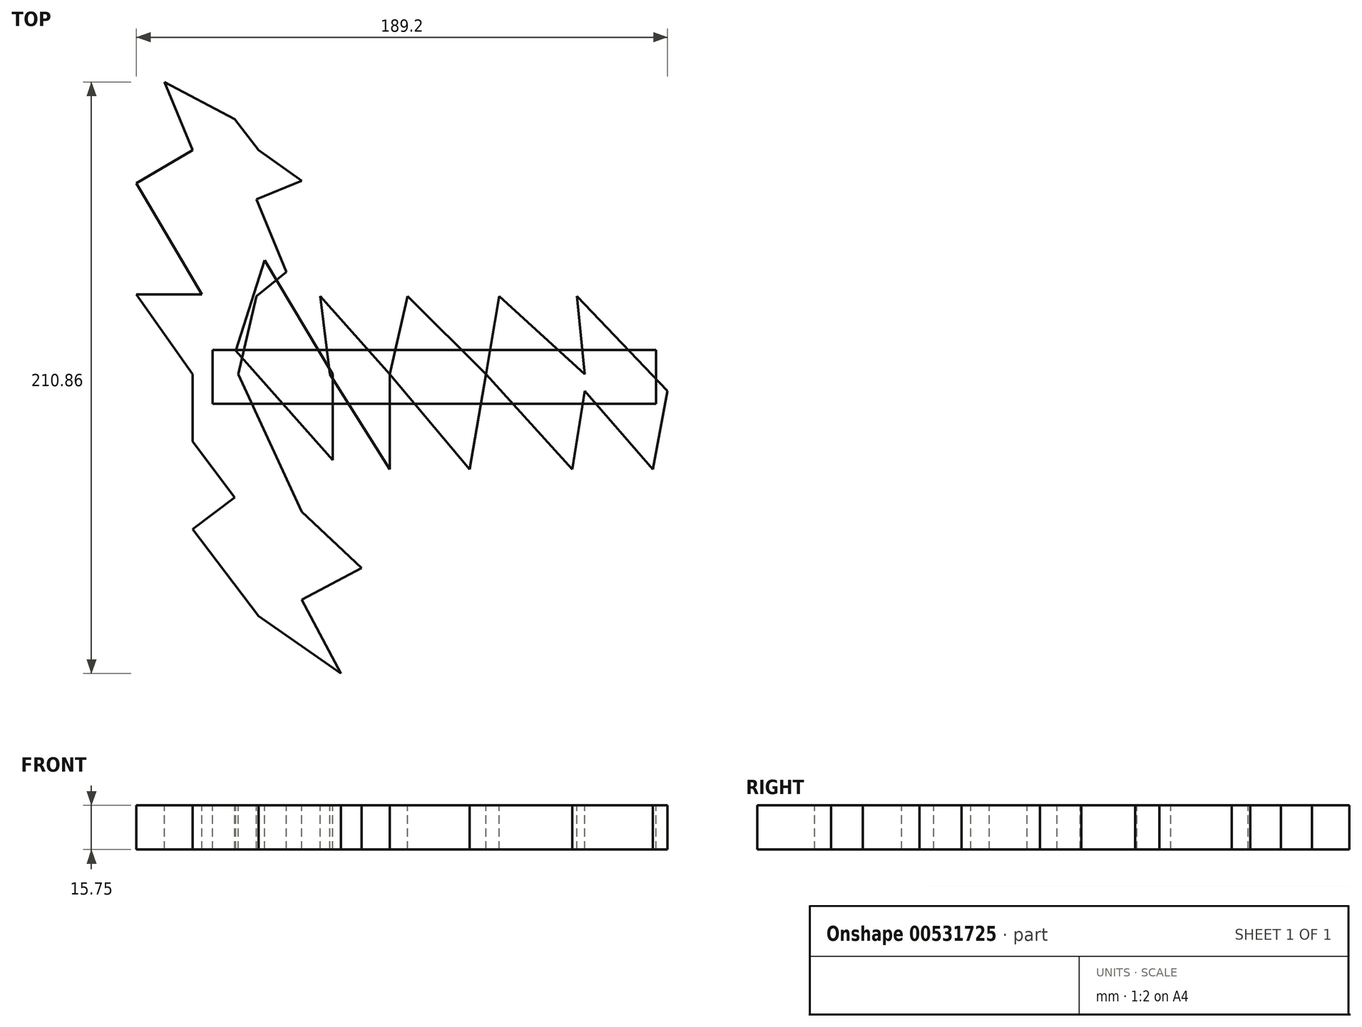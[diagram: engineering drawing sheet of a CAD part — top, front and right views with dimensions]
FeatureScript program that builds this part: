
annotation { "Feature Type Name" : "Feature", "Feature Type Description" : "" }
export const myFeature = defineFeature(function(context is Context, id is Id, definition is map)
    precondition{}
    {
        {
            var Q0;
            Q0=qCreatedBy(makeId("Top.planeOp"),FACE);
            var sketch = newSketch(context, id + "F0", { "sketchPlane" : qUnion([Q0])});
            skLineSegment(sketch, "E0", {"start": v(-17.17, 0) * mm, "end": v(5.55, -23.65) * mm});
            skLineSegment(sketch, "E1", {"start": v(5.55, -23.65) * mm, "end": v(15.57, 0) * mm});
            skLineSegment(sketch, "E2", {"start": v(15.57, 0) * mm, "end": v(36.83, -33.96) * mm});
            skLineSegment(sketch, "E3", {"start": v(36.83, -33.96) * mm, "end": v(36.83, 0) * mm});
            skLineSegment(sketch, "E4", {"start": v(36.83, 0) * mm, "end": v(65.33, -33.96) * mm});
            skLineSegment(sketch, "E5", {"start": v(65.33, -33.96) * mm, "end": v(71.14, 0) * mm});
            skLineSegment(sketch, "E6", {"start": v(71.14, 0) * mm, "end": v(101.81, -33.96) * mm});
            skLineSegment(sketch, "E7", {"start": v(101.81, -33.96) * mm, "end": v(106.3, -6) * mm});
            skLineSegment(sketch, "E8", {"start": v(106.3, -6) * mm, "end": v(130.57, -33.96) * mm});
            skLineSegment(sketch, "E9", {"start": v(130.57, -33.96) * mm, "end": v(135.8, -6) * mm});
            skLineSegment(sketch, "E10", {"start": v(135.8, -6) * mm, "end": v(103.49, 27.83) * mm});
            skLineSegment(sketch, "E11", {"start": v(103.49, 27.83) * mm, "end": v(106.3, 0) * mm});
            skLineSegment(sketch, "E12", {"start": v(106.3, 0) * mm, "end": v(75.83, 27.83) * mm});
            skLineSegment(sketch, "E13", {"start": v(75.83, 27.83) * mm, "end": v(71.14, 0) * mm});
            skLineSegment(sketch, "E14", {"start": v(71.14, 0) * mm, "end": v(43.24, 27.83) * mm});
            skLineSegment(sketch, "E15", {"start": v(43.24, 27.83) * mm, "end": v(36.83, 0) * mm});
            skLineSegment(sketch, "E16", {"start": v(36.83, 0) * mm, "end": v(12.02, 27.83) * mm});
            skLineSegment(sketch, "E17", {"start": v(12.02, 27.83) * mm, "end": v(15.57, 0) * mm});
            skLineSegment(sketch, "E18", {"start": v(12.02, 0) * mm, "end": v(-10.6, 27.83) * mm});
            skLineSegment(sketch, "E19", {"start": v(-10.6, 27.83) * mm, "end": v(-17.17, 0) * mm});
            skLineSegment(sketch, "E20", {"start": v(-17.17, 0) * mm, "end": v(5.5, -49) * mm});
            skLineSegment(sketch, "E21", {"start": v(5.5, -49) * mm, "end": v(26.75, -69.15) * mm});
            skLineSegment(sketch, "E22", {"start": v(26.75, -69.15) * mm, "end": v(5.5, -80.46) * mm});
            skLineSegment(sketch, "E23", {"start": v(5.5, -80.46) * mm, "end": v(19.47, -106.74) * mm});
            skLineSegment(sketch, "E24", {"start": v(19.47, -106.74) * mm, "end": v(-9.96, -86.3) * mm});
            skLineSegment(sketch, "E25", {"start": v(-9.96, -86.3) * mm, "end": v(-33.44, -55.27) * mm});
            skLineSegment(sketch, "E26", {"start": v(-33.44, -55.27) * mm, "end": v(-18.43, -43.9) * mm});
            skLineSegment(sketch, "E27", {"start": v(-18.43, -43.9) * mm, "end": v(-33.44, -24.08) * mm});
            skLineSegment(sketch, "E28", {"start": v(-33.44, -24.08) * mm, "end": v(-33.44, 0) * mm});
            skLineSegment(sketch, "E29", {"start": v(-33.44, 0) * mm, "end": v(-53.4, 28.44) * mm});
            skLineSegment(sketch, "E30", {"start": v(-53.4, 28.44) * mm, "end": v(-30.08, 28.44) * mm});
            skLineSegment(sketch, "E31", {"start": v(-30.08, 28.44) * mm, "end": v(-53.4, 68.06) * mm});
            skLineSegment(sketch, "E32", {"start": v(-53.4, 68.06) * mm, "end": v(-33.44, 79.82) * mm});
            skLineSegment(sketch, "E33", {"start": v(-33.44, 79.82) * mm, "end": v(-43.4, 104.12) * mm});
            skLineSegment(sketch, "E34", {"start": v(-43.4, 104.12) * mm, "end": v(-18.43, 90.85) * mm});
            skLineSegment(sketch, "E35", {"start": v(-18.43, 90.85) * mm, "end": v(-33.44, 79.82) * mm});
            skLineSegment(sketch, "E36", {"start": v(-30.08, 28.44) * mm, "end": v(-33.44, 79.82) * mm});
            skLineSegment(sketch, "E37", {"start": v(-10.6, 27.83) * mm, "end": v(0, 36.45) * mm});
            skLineSegment(sketch, "E38", {"start": v(0, 36.45) * mm, "end": v(-10.6, 62.33) * mm});
            skLineSegment(sketch, "E39", {"start": v(-10.6, 62.33) * mm, "end": v(5.5, 68.93) * mm});
            skLineSegment(sketch, "E40", {"start": v(5.5, 68.93) * mm, "end": v(-9.96, 79.82) * mm});
            skLineSegment(sketch, "E41", {"start": v(-9.96, 79.82) * mm, "end": v(-18.43, 90.85) * mm});
            skSolve(sketch);
        }
        {
            var Q0;
            Q0=makeQuery(id+"F0.imprint","IMPRINT",FACE,{"disambiguationData":[TD([[makeQuery(id+"F0.imprint","IMPRINT",EDGE,{"derivedFrom":sQuery(id+"F0.wireOp",EDGE,"E19")}),-1.0]])]});
            var Q1;
            Q1=makeQuery(id+"F0.imprint","IMPRINT",FACE,{"disambiguationData":[TD([[makeQuery(id+"F0.imprint","IMPRINT",EDGE,{"derivedFrom":sQuery(id+"F0.wireOp",EDGE,"E31")}),-1.0]])]});
            var Q2;
            Q2=makeQuery(id+"F0.imprint","IMPRINT",FACE,{"disambiguationData":[TD([[makeQuery(id+"F0.imprint","IMPRINT",EDGE,{"derivedFrom":sQuery(id+"F0.wireOp",EDGE,"E33")}),-1.0]])]});
            var Q3;
            Q3=makeQuery(id+"F0.imprint","IMPRINT",FACE,{"disambiguationData":[TD([[makeQuery(id+"F0.imprint","IMPRINT",EDGE,{"derivedFrom":sQuery(id+"F0.wireOp",EDGE,"E2")}),1.0]])]});
            var Q4;
            Q4=makeQuery(id+"F0.imprint","IMPRINT",FACE,{"disambiguationData":[TD([[makeQuery(id+"F0.imprint","IMPRINT",EDGE,{"derivedFrom":sQuery(id+"F0.wireOp",EDGE,"E4")}),1.0]])]});
            var Q5;
            Q5=makeQuery(id+"F0.imprint","IMPRINT",FACE,{"disambiguationData":[TD([[makeQuery(id+"F0.imprint","IMPRINT",EDGE,{"derivedFrom":sQuery(id+"F0.wireOp",EDGE,"E6")}),1.0]])]});
            extrude(context, id + "F1", {"entities" : qUnion([Q0, Q1, Q2, Q3, Q4, Q5]), "oppositeDirection" : true, "depth" : 15.75 * mm, "offsetDistance" : 25.4 * mm});
        }
        {
            var Q0;
            Q0=qCreatedBy(makeId("Top.planeOp"),FACE);
            var sketch = newSketch(context, id + "F2", { "sketchPlane" : qUnion([Q0])});
            skLineSegment(sketch, "E42", {"start": v(16.56, 0) * mm, "end": v(16.56, -30.69) * mm});
            skLineSegment(sketch, "E43", {"start": v(16.56, -30.69) * mm, "end": v(-18, 8.35) * mm});
            skLineSegment(sketch, "E44", {"start": v(-18, 8.35) * mm, "end": v(16.56, 0) * mm});
            skLineSegment(sketch, "E45", {"start": v(16.56, 0) * mm, "end": v(-7.74, 40.62) * mm});
            skLineSegment(sketch, "E46", {"start": v(-7.74, 40.62) * mm, "end": v(-18, 8.35) * mm});
            skSolve(sketch);
        }
        {
            var Q0;
            Q0=makeQuery(id+"F2.imprint","IMPRINT",FACE,{"disambiguationData":[TD([[makeQuery(id+"F2.imprint","IMPRINT",EDGE,{"derivedFrom":sQuery(id+"F2.wireOp",EDGE,"E42")}),-1.0]])]});
            var Q1;
            Q1=makeQuery(id+"F2.imprint","IMPRINT",FACE,{"disambiguationData":[TD([[makeQuery(id+"F2.imprint","IMPRINT",EDGE,{"derivedFrom":sQuery(id+"F2.wireOp",EDGE,"E44")}),1.0]])]});
            extrude(context, id + "F3", {"entities" : qUnion([Q0, Q1]), "oppositeDirection" : true, "depth" : 15.75 * mm, "offsetDistance" : 25.4 * mm});
        }
        {
            var Q0;
            Q0=qCreatedBy(makeId("Top.planeOp"),FACE);
            var sketch = newSketch(context, id + "F4", { "sketchPlane" : qUnion([Q0])});
            skLineSegment(sketch, "E47.bottom", {"start": v(-26.27, 8.64) * mm, "end": v(131.74, 8.64) * mm});
            skLineSegment(sketch, "E47.top", {"start": v(-26.27, -10.57) * mm, "end": v(131.74, -10.57) * mm});
            skLineSegment(sketch, "E47.left", {"start": v(-26.27, 8.64) * mm, "end": v(-26.27, -10.57) * mm});
            skLineSegment(sketch, "E47.right", {"start": v(131.74, 8.64) * mm, "end": v(131.74, -10.57) * mm});
            skSolve(sketch);
        }
        {
            var Q0;
            Q0=makeQuery(id+"F4.imprint","IMPRINT",FACE,{"disambiguationData":[TD([[makeQuery(id+"F4.imprint","IMPRINT",EDGE,{"derivedFrom":sQuery(id+"F4.wireOp",EDGE,"E47.bottom")}),-1.0]])]});
            extrude(context, id + "F5", {"entities" : qUnion([Q0]), "oppositeDirection" : true, "depth" : 15.75 * mm, "offsetDistance" : 25.4 * mm});
        }
    });
